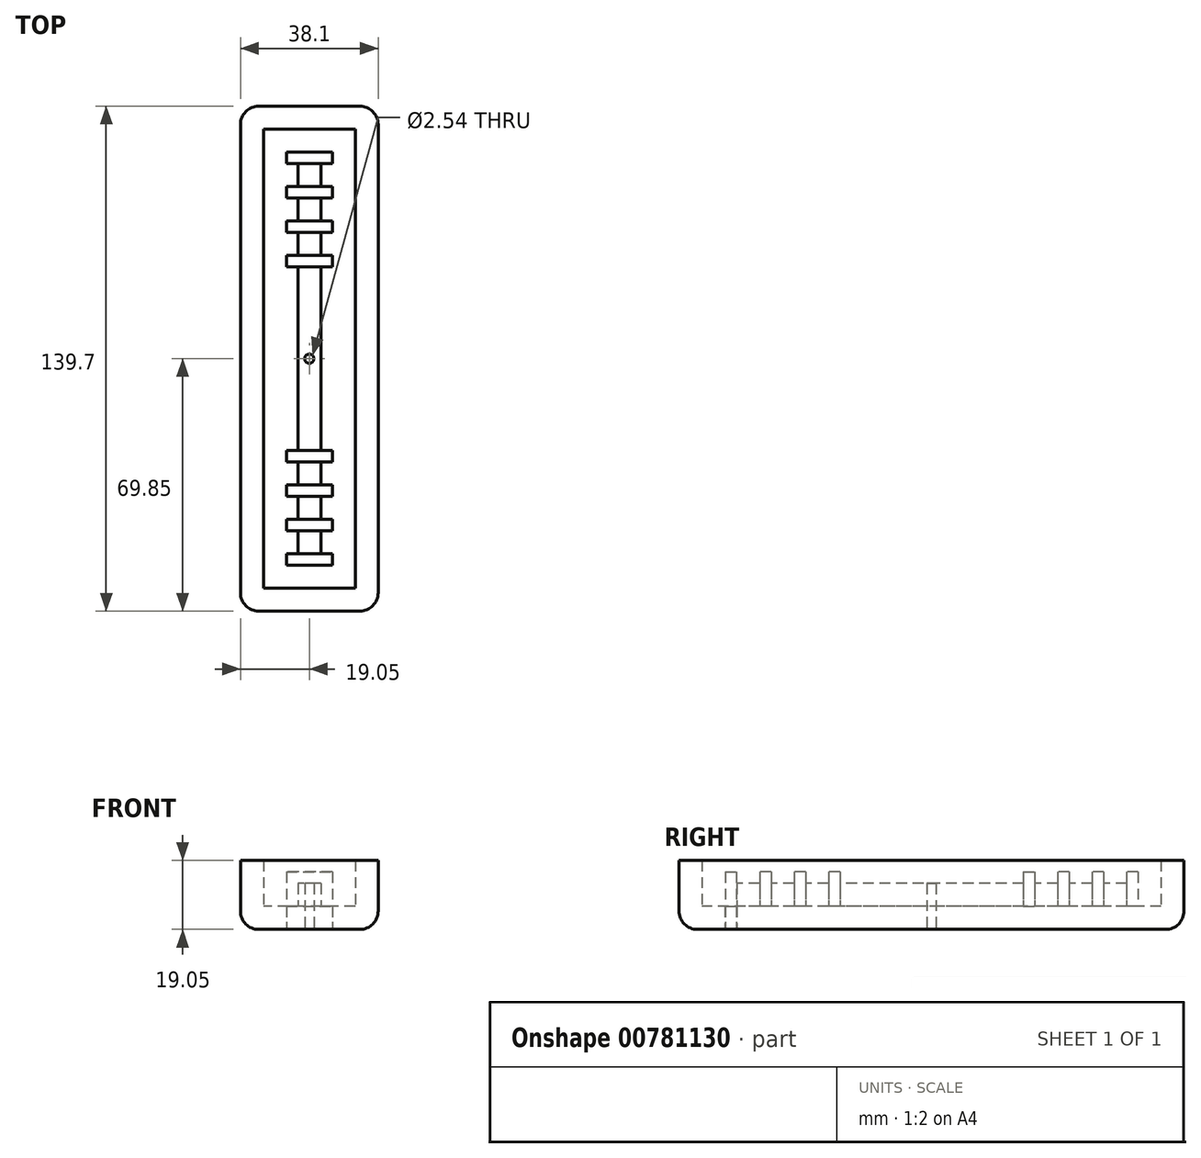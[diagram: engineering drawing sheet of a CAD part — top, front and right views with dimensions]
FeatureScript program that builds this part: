
annotation { "Feature Type Name" : "Feature", "Feature Type Description" : "" }
export const myFeature = defineFeature(function(context is Context, id is Id, definition is map)
    precondition{}
    {
        {
            var Q0;
            Q0=qCreatedBy(makeId("Top.planeOp"),FACE);
            var sketch = newSketch(context, id + "F0", { "sketchPlane" : qUnion([Q0])});
            skLineSegment(sketch, "E0.bottom", {"start": v(12.7, 63.5) * mm, "end": v(-12.7, 63.5) * mm});
            skLineSegment(sketch, "E0.top", {"start": v(12.7, -63.5) * mm, "end": v(-12.7, -63.5) * mm});
            skLineSegment(sketch, "E0.left", {"start": v(12.7, 63.5) * mm, "end": v(12.7, -63.5) * mm});
            skLineSegment(sketch, "E0.right", {"start": v(-12.7, 63.5) * mm, "end": v(-12.7, -63.5) * mm});
            skPoint(sketch, "E0.middle", {"position": v(0, 0) * mm});
            skLineSegment(sketch, "E1.bottom", {"start": v(19.05, 69.85) * mm, "end": v(-19.05, 69.85) * mm});
            skLineSegment(sketch, "E1.top", {"start": v(19.05, -69.85) * mm, "end": v(-19.05, -69.85) * mm});
            skLineSegment(sketch, "E1.left", {"start": v(19.05, 69.85) * mm, "end": v(19.05, -69.85) * mm});
            skLineSegment(sketch, "E1.right", {"start": v(-19.05, 69.85) * mm, "end": v(-19.05, -69.85) * mm});
            skLineSegment(sketch, "E2.bottom", {"start": v(3.18, 57.15) * mm, "end": v(-3.18, 57.15) * mm});
            skLineSegment(sketch, "E2.top", {"start": v(3.18, -57.15) * mm, "end": v(-3.18, -57.15) * mm});
            skLineSegment(sketch, "E2.left", {"start": v(3.18, 57.15) * mm, "end": v(3.18, -57.15) * mm});
            skLineSegment(sketch, "E2.right", {"start": v(-3.18, 57.15) * mm, "end": v(-3.18, -57.15) * mm});
            skLineSegment(sketch, "E3.bottom", {"start": v(6.35, 57.15) * mm, "end": v(-6.35, 57.15) * mm});
            skLineSegment(sketch, "E3.top", {"start": v(6.35, 53.98) * mm, "end": v(-6.35, 53.98) * mm});
            skLineSegment(sketch, "E3.left", {"start": v(6.35, 57.15) * mm, "end": v(6.35, 53.98) * mm});
            skLineSegment(sketch, "E3.right", {"start": v(-6.35, 57.15) * mm, "end": v(-6.35, 53.98) * mm});
            skPoint(sketch, "E3.middle", {"position": v(0, 55.56) * mm});
            skPoint(sketch, "E3.middle.positionSnap0", {"position": v(0, 57.15) * mm});
            skPoint(sketch, "E3.centerSnap0", {"position": v(0, 57.15) * mm});
            skLineSegment(sketch, "E4.bottom", {"start": v(-6.35, -57.15) * mm, "end": v(6.35, -57.15) * mm});
            skLineSegment(sketch, "E4.top", {"start": v(-6.35, -53.98) * mm, "end": v(6.35, -53.98) * mm});
            skLineSegment(sketch, "E4.left", {"start": v(-6.35, -57.15) * mm, "end": v(-6.35, -53.98) * mm});
            skLineSegment(sketch, "E4.right", {"start": v(6.35, -57.15) * mm, "end": v(6.35, -53.98) * mm});
            skPoint(sketch, "E4.middle", {"position": v(0, -55.56) * mm});
            skLineSegment(sketch, "E5.bottom", {"start": v(-6.35, 47.63) * mm, "end": v(6.35, 47.63) * mm});
            skLineSegment(sketch, "E5.top", {"start": v(-6.35, 44.45) * mm, "end": v(6.35, 44.45) * mm});
            skLineSegment(sketch, "E5.left", {"start": v(-6.35, 47.63) * mm, "end": v(-6.35, 44.45) * mm});
            skLineSegment(sketch, "E5.right", {"start": v(6.35, 47.63) * mm, "end": v(6.35, 44.45) * mm});
            skPoint(sketch, "E5.middle", {"position": v(0, 46.04) * mm});
            skLineSegment(sketch, "E6", {"start": v(3.18, 53.98) * mm, "end": v(3.18, 47.63) * mm});
            skLineSegment(sketch, "E7.bottom", {"start": v(6.35, 38.1) * mm, "end": v(-6.35, 38.1) * mm});
            skLineSegment(sketch, "E7.top", {"start": v(6.35, 34.93) * mm, "end": v(-6.35, 34.93) * mm});
            skLineSegment(sketch, "E7.left", {"start": v(6.35, 38.1) * mm, "end": v(6.35, 34.93) * mm});
            skLineSegment(sketch, "E7.right", {"start": v(-6.35, 38.1) * mm, "end": v(-6.35, 34.93) * mm});
            skPoint(sketch, "E7.middle", {"position": v(0, 36.51) * mm});
            skLineSegment(sketch, "E8", {"start": v(3.18, 44.45) * mm, "end": v(3.18, 38.1) * mm});
            skLineSegment(sketch, "E9.bottom", {"start": v(6.35, 25.4) * mm, "end": v(-6.35, 25.4) * mm});
            skLineSegment(sketch, "E9.top", {"start": v(6.35, 28.58) * mm, "end": v(-6.35, 28.58) * mm});
            skLineSegment(sketch, "E9.left", {"start": v(6.35, 25.4) * mm, "end": v(6.35, 28.58) * mm});
            skLineSegment(sketch, "E9.right", {"start": v(-6.35, 25.4) * mm, "end": v(-6.35, 28.58) * mm});
            skPoint(sketch, "E9.middle", {"position": v(0, 26.99) * mm});
            skLineSegment(sketch, "E10", {"start": v(3.18, 34.93) * mm, "end": v(3.18, 28.58) * mm});
            skLineSegment(sketch, "E11.bottom", {"start": v(6.38, -25.35) * mm, "end": v(-6.32, -25.35) * mm});
            skLineSegment(sketch, "E11.top", {"start": v(6.38, -28.53) * mm, "end": v(-6.32, -28.53) * mm});
            skLineSegment(sketch, "E11.left", {"start": v(6.38, -25.35) * mm, "end": v(6.38, -28.53) * mm});
            skLineSegment(sketch, "E11.right", {"start": v(-6.32, -25.35) * mm, "end": v(-6.32, -28.53) * mm});
            skLineSegment(sketch, "E12.bottom", {"start": v(-6.32, -34.88) * mm, "end": v(6.38, -34.88) * mm});
            skLineSegment(sketch, "E12.top", {"start": v(-6.32, -38.05) * mm, "end": v(6.38, -38.05) * mm});
            skLineSegment(sketch, "E12.left", {"start": v(-6.32, -34.88) * mm, "end": v(-6.32, -38.05) * mm});
            skLineSegment(sketch, "E12.right", {"start": v(6.38, -34.88) * mm, "end": v(6.38, -38.05) * mm});
            skLineSegment(sketch, "E13.bottom", {"start": v(6.38, -44.4) * mm, "end": v(-6.32, -44.4) * mm});
            skLineSegment(sketch, "E13.top", {"start": v(6.38, -47.58) * mm, "end": v(-6.32, -47.58) * mm});
            skLineSegment(sketch, "E13.left", {"start": v(6.38, -44.4) * mm, "end": v(6.38, -47.58) * mm});
            skLineSegment(sketch, "E13.right", {"start": v(-6.32, -44.4) * mm, "end": v(-6.32, -47.58) * mm});
            skLineSegment(sketch, "E14.bottom", {"start": v(6.38, -57.1) * mm, "end": v(-6.32, -57.1) * mm});
            skLineSegment(sketch, "E14.top", {"start": v(6.38, -53.93) * mm, "end": v(-6.32, -53.93) * mm});
            skLineSegment(sketch, "E14.left", {"start": v(6.38, -57.1) * mm, "end": v(6.38, -53.93) * mm});
            skLineSegment(sketch, "E14.right", {"start": v(-6.32, -57.1) * mm, "end": v(-6.32, -53.93) * mm});
            skCircle(sketch, "E15", {"center": v(0, 0) * mm, "radius": 1.27 * mm});
            skSolve(sketch);
        }
        {
            var Q0;
            Q0=makeQuery(id+"F0.imprint","IMPRINT",FACE,{"disambiguationData":[TD([[makeQuery(id+"F0.imprint","IMPRINT",EDGE,{"derivedFrom":sQuery(id+"F0.wireOp",EDGE,"E0.bottom")}),-1.0]])]});
            extrude(context, id + "F1", {"entities" : qUnion([Q0]), "depth" : 19.05 * mm, "offsetDistance" : 25.4 * mm});
        }
        {
            var Q0;
            Q0=makeQuery(id+"F0.imprint","IMPRINT",FACE,{"disambiguationData":[TD([[makeQuery(id+"F0.imprint","IMPRINT",EDGE,{"derivedFrom":sQuery(id+"F0.wireOp",EDGE,"E0.bottom")}),1.0]])]});
            extrude(context, id + "F2", {"entities" : qUnion([Q0]), "operationType" : NewBodyOperationType.ADD, "depth" : 6.35 * mm, "offsetDistance" : 25.4 * mm});
        }
        {
            var Q0;
            Q0=makeQuery(id+"F0.imprint","IMPRINT",FACE,{"disambiguationData":[TD([[makeQuery(id+"F0.imprint","IMPRINT",EDGE,{"derivedFrom":sQuery(id+"F0.wireOp",EDGE,"E15")}),-1.0]])]});
            var Q1;
            {var subQ0=sQuery(id+"F0.wireOp",EDGE,"E7.top");var subQ1=sQuery(id+"F0.wireOp",EDGE,"E2.left");var subQ2=makeQuery(id+"F0.imprint","INTERSECT",VERTEX,{"derivedFrom":[subQ1,subQ0]});Q1=makeQuery(id+"F0.imprint","IMPRINT",FACE,{"disambiguationData":[TD([[makeQuery(id+"F0.imprint","IMPRINT",EDGE,{"disambiguationData":[TD([[subQ2,-1.0]])],"derivedFrom":subQ1}),-1.0]])]});}
            var Q2;
            {var subQ0=sQuery(id+"F0.wireOp",EDGE,"E7.bottom");var subQ1=sQuery(id+"F0.wireOp",EDGE,"E2.left");var subQ2=makeQuery(id+"F0.imprint","INTERSECT",VERTEX,{"derivedFrom":[subQ1,subQ0]});Q2=makeQuery(id+"F0.imprint","IMPRINT",FACE,{"disambiguationData":[TD([[makeQuery(id+"F0.imprint","IMPRINT",EDGE,{"disambiguationData":[TD([[subQ2,1.0]])],"derivedFrom":subQ1}),-1.0]])]});}
            var Q3;
            {var subQ0=sQuery(id+"F0.wireOp",EDGE,"E3.top");var subQ1=sQuery(id+"F0.wireOp",EDGE,"E2.left");var subQ2=makeQuery(id+"F0.imprint","INTERSECT",VERTEX,{"derivedFrom":[subQ1,subQ0]});Q3=makeQuery(id+"F0.imprint","IMPRINT",FACE,{"disambiguationData":[TD([[makeQuery(id+"F0.imprint","IMPRINT",EDGE,{"disambiguationData":[TD([[subQ2,-1.0]])],"derivedFrom":subQ1}),-1.0]])]});}
            var Q4;
            {var subQ0=sQuery(id+"F0.wireOp",EDGE,"E11.top");var subQ1=sQuery(id+"F0.wireOp",EDGE,"E2.left");var subQ2=makeQuery(id+"F0.imprint","INTERSECT",VERTEX,{"derivedFrom":[subQ1,subQ0]});Q4=makeQuery(id+"F0.imprint","IMPRINT",FACE,{"disambiguationData":[TD([[makeQuery(id+"F0.imprint","IMPRINT",EDGE,{"disambiguationData":[TD([[subQ2,-1.0]])],"derivedFrom":subQ1}),-1.0]])]});}
            var Q5;
            {var subQ0=sQuery(id+"F0.wireOp",EDGE,"E13.bottom");var subQ1=sQuery(id+"F0.wireOp",EDGE,"E2.left");var subQ2=makeQuery(id+"F0.imprint","INTERSECT",VERTEX,{"derivedFrom":[subQ1,subQ0]});Q5=makeQuery(id+"F0.imprint","IMPRINT",FACE,{"disambiguationData":[TD([[makeQuery(id+"F0.imprint","IMPRINT",EDGE,{"disambiguationData":[TD([[subQ2,1.0]])],"derivedFrom":subQ1}),-1.0]])]});}
            var Q6;
            {var subQ0=sQuery(id+"F0.wireOp",EDGE,"E13.top");var subQ1=sQuery(id+"F0.wireOp",EDGE,"E2.left");var subQ2=makeQuery(id+"F0.imprint","INTERSECT",VERTEX,{"derivedFrom":[subQ1,subQ0]});Q6=makeQuery(id+"F0.imprint","IMPRINT",FACE,{"disambiguationData":[TD([[makeQuery(id+"F0.imprint","IMPRINT",EDGE,{"disambiguationData":[TD([[subQ2,-1.0]])],"derivedFrom":subQ1}),-1.0]])]});}
            extrude(context, id + "F3", {"entities" : qUnion([Q0, Q1, Q2, Q3, Q4, Q5, Q6]), "operationType" : NewBodyOperationType.ADD, "depth" : 12.7 * mm, "offsetDistance" : 25.4 * mm});
        }
        {
            var Q0;
            {var subQ0=sQuery(id+"F0.wireOp",EDGE,"E2.bottom");Q0=makeQuery(id+"F0.imprint","IMPRINT",FACE,{"disambiguationData":[TD([[makeQuery(id+"F0.imprint","IMPRINT",EDGE,{"derivedFrom":subQ0}),1.0]])]});}
            var Q1;
            {var subQ5=sQuery(id+"F0.wireOp",EDGE,"E3.left");Q1=makeQuery(id+"F0.imprint","IMPRINT",FACE,{"disambiguationData":[TD([[makeQuery(id+"F0.imprint","IMPRINT",EDGE,{"derivedFrom":subQ5}),-1.0]])]});}
            var Q2;
            {var subQ5=sQuery(id+"F0.wireOp",EDGE,"E3.right");Q2=makeQuery(id+"F0.imprint","IMPRINT",FACE,{"disambiguationData":[TD([[makeQuery(id+"F0.imprint","IMPRINT",EDGE,{"derivedFrom":subQ5}),1.0]])]});}
            var Q3;
            {var subQ5=sQuery(id+"F0.wireOp",EDGE,"E5.left");Q3=makeQuery(id+"F0.imprint","IMPRINT",FACE,{"disambiguationData":[TD([[makeQuery(id+"F0.imprint","IMPRINT",EDGE,{"derivedFrom":subQ5}),1.0]])]});}
            var Q4;
            {var subQ0=sQuery(id+"F0.wireOp",EDGE,"E5.top");var subQ1=sQuery(id+"F0.wireOp",EDGE,"E2.left");var subQ2=makeQuery(id+"F0.imprint","INTERSECT",VERTEX,{"derivedFrom":[subQ1,subQ0]});Q4=makeQuery(id+"F0.imprint","IMPRINT",FACE,{"disambiguationData":[TD([[makeQuery(id+"F0.imprint","IMPRINT",EDGE,{"disambiguationData":[TD([[subQ2,1.0]])],"derivedFrom":subQ1}),-1.0]])]});}
            var Q5;
            {var subQ5=sQuery(id+"F0.wireOp",EDGE,"E5.right");Q5=makeQuery(id+"F0.imprint","IMPRINT",FACE,{"disambiguationData":[TD([[makeQuery(id+"F0.imprint","IMPRINT",EDGE,{"derivedFrom":subQ5}),-1.0]])]});}
            var Q6;
            {var subQ5=sQuery(id+"F0.wireOp",EDGE,"E7.left");Q6=makeQuery(id+"F0.imprint","IMPRINT",FACE,{"disambiguationData":[TD([[makeQuery(id+"F0.imprint","IMPRINT",EDGE,{"derivedFrom":subQ5}),-1.0]])]});}
            var Q7;
            {var subQ0=sQuery(id+"F0.wireOp",EDGE,"E7.bottom");var subQ1=sQuery(id+"F0.wireOp",EDGE,"E2.left");var subQ2=makeQuery(id+"F0.imprint","INTERSECT",VERTEX,{"derivedFrom":[subQ1,subQ0]});Q7=makeQuery(id+"F0.imprint","IMPRINT",FACE,{"disambiguationData":[TD([[makeQuery(id+"F0.imprint","IMPRINT",EDGE,{"disambiguationData":[TD([[subQ2,-1.0]])],"derivedFrom":subQ1}),-1.0]])]});}
            var Q8;
            {var subQ5=sQuery(id+"F0.wireOp",EDGE,"E7.right");Q8=makeQuery(id+"F0.imprint","IMPRINT",FACE,{"disambiguationData":[TD([[makeQuery(id+"F0.imprint","IMPRINT",EDGE,{"derivedFrom":subQ5}),1.0]])]});}
            var Q9;
            {var subQ5=sQuery(id+"F0.wireOp",EDGE,"E9.right");Q9=makeQuery(id+"F0.imprint","IMPRINT",FACE,{"disambiguationData":[TD([[makeQuery(id+"F0.imprint","IMPRINT",EDGE,{"derivedFrom":subQ5}),-1.0]])]});}
            var Q10;
            {var subQ0=sQuery(id+"F0.wireOp",EDGE,"E9.bottom");var subQ1=sQuery(id+"F0.wireOp",EDGE,"E2.left");var subQ2=makeQuery(id+"F0.imprint","INTERSECT",VERTEX,{"derivedFrom":[subQ1,subQ0]});Q10=makeQuery(id+"F0.imprint","IMPRINT",FACE,{"disambiguationData":[TD([[makeQuery(id+"F0.imprint","IMPRINT",EDGE,{"disambiguationData":[TD([[subQ2,1.0]])],"derivedFrom":subQ1}),-1.0]])]});}
            var Q11;
            {var subQ5=sQuery(id+"F0.wireOp",EDGE,"E9.left");Q11=makeQuery(id+"F0.imprint","IMPRINT",FACE,{"disambiguationData":[TD([[makeQuery(id+"F0.imprint","IMPRINT",EDGE,{"derivedFrom":subQ5}),1.0]])]});}
            var Q12;
            {var subQ0=sQuery(id+"F0.wireOp",EDGE,"E11.bottom");var subQ1=sQuery(id+"F0.wireOp",EDGE,"E2.left");var subQ2=makeQuery(id+"F0.imprint","INTERSECT",VERTEX,{"derivedFrom":[subQ1,subQ0]});Q12=makeQuery(id+"F0.imprint","IMPRINT",FACE,{"disambiguationData":[TD([[makeQuery(id+"F0.imprint","IMPRINT",EDGE,{"disambiguationData":[TD([[subQ2,-1.0]])],"derivedFrom":subQ1}),-1.0]])]});}
            var Q13;
            {var subQ5=sQuery(id+"F0.wireOp",EDGE,"E11.right");Q13=makeQuery(id+"F0.imprint","IMPRINT",FACE,{"disambiguationData":[TD([[makeQuery(id+"F0.imprint","IMPRINT",EDGE,{"derivedFrom":subQ5}),1.0]])]});}
            var Q14;
            {var subQ5=sQuery(id+"F0.wireOp",EDGE,"E11.left");Q14=makeQuery(id+"F0.imprint","IMPRINT",FACE,{"disambiguationData":[TD([[makeQuery(id+"F0.imprint","IMPRINT",EDGE,{"derivedFrom":subQ5}),-1.0]])]});}
            var Q15;
            {var subQ5=sQuery(id+"F0.wireOp",EDGE,"E12.right");Q15=makeQuery(id+"F0.imprint","IMPRINT",FACE,{"disambiguationData":[TD([[makeQuery(id+"F0.imprint","IMPRINT",EDGE,{"derivedFrom":subQ5}),-1.0]])]});}
            var Q16;
            {var subQ0=sQuery(id+"F0.wireOp",EDGE,"E12.bottom");var subQ1=sQuery(id+"F0.wireOp",EDGE,"E2.left");var subQ2=makeQuery(id+"F0.imprint","INTERSECT",VERTEX,{"derivedFrom":[subQ1,subQ0]});Q16=makeQuery(id+"F0.imprint","IMPRINT",FACE,{"disambiguationData":[TD([[makeQuery(id+"F0.imprint","IMPRINT",EDGE,{"disambiguationData":[TD([[subQ2,-1.0]])],"derivedFrom":subQ1}),-1.0]])]});}
            var Q17;
            {var subQ5=sQuery(id+"F0.wireOp",EDGE,"E12.left");Q17=makeQuery(id+"F0.imprint","IMPRINT",FACE,{"disambiguationData":[TD([[makeQuery(id+"F0.imprint","IMPRINT",EDGE,{"derivedFrom":subQ5}),1.0]])]});}
            var Q18;
            {var subQ0=sQuery(id+"F0.wireOp",EDGE,"E13.bottom");var subQ1=sQuery(id+"F0.wireOp",EDGE,"E2.left");var subQ2=makeQuery(id+"F0.imprint","INTERSECT",VERTEX,{"derivedFrom":[subQ1,subQ0]});Q18=makeQuery(id+"F0.imprint","IMPRINT",FACE,{"disambiguationData":[TD([[makeQuery(id+"F0.imprint","IMPRINT",EDGE,{"disambiguationData":[TD([[subQ2,-1.0]])],"derivedFrom":subQ1}),-1.0]])]});}
            var Q19;
            {var subQ0=sQuery(id+"F0.wireOp",EDGE,"E4.top");var subQ1=sQuery(id+"F0.wireOp",EDGE,"E2.left");var subQ2=makeQuery(id+"F0.imprint","INTERSECT",VERTEX,{"derivedFrom":[subQ1,subQ0]});Q19=makeQuery(id+"F0.imprint","IMPRINT",FACE,{"disambiguationData":[TD([[makeQuery(id+"F0.imprint","IMPRINT",EDGE,{"disambiguationData":[TD([[subQ2,-1.0]])],"derivedFrom":subQ1}),-1.0]])]});}
            var Q20;
            {var subQ5=sQuery(id+"F0.wireOp",EDGE,"E13.left");Q20=makeQuery(id+"F0.imprint","IMPRINT",FACE,{"disambiguationData":[TD([[makeQuery(id+"F0.imprint","IMPRINT",EDGE,{"derivedFrom":subQ5}),-1.0]])]});}
            var Q21;
            {var subQ0=sQuery(id+"F0.wireOp",EDGE,"E4.top");var subQ1=sQuery(id+"F0.wireOp",EDGE,"E2.left");var subQ2=makeQuery(id+"F0.imprint","INTERSECT",VERTEX,{"derivedFrom":[subQ1,subQ0]});Q21=makeQuery(id+"F0.imprint","IMPRINT",FACE,{"disambiguationData":[TD([[makeQuery(id+"F0.imprint","IMPRINT",EDGE,{"disambiguationData":[TD([[subQ2,-1.0]])],"derivedFrom":subQ1}),1.0]])]});}
            var Q22;
            {var subQ0=sQuery(id+"F0.wireOp",EDGE,"E4.top");var subQ1=sQuery(id+"F0.wireOp",EDGE,"E2.right");var subQ2=makeQuery(id+"F0.imprint","INTERSECT",VERTEX,{"derivedFrom":[subQ1,subQ0]});Q22=makeQuery(id+"F0.imprint","IMPRINT",FACE,{"disambiguationData":[TD([[makeQuery(id+"F0.imprint","IMPRINT",EDGE,{"disambiguationData":[TD([[subQ2,-1.0]])],"derivedFrom":subQ1}),-1.0]])]});}
            var Q23;
            {var subQ5=sQuery(id+"F0.wireOp",EDGE,"E13.right");Q23=makeQuery(id+"F0.imprint","IMPRINT",FACE,{"disambiguationData":[TD([[makeQuery(id+"F0.imprint","IMPRINT",EDGE,{"derivedFrom":subQ5}),1.0]])]});}
            extrude(context, id + "F4", {"entities" : qUnion([Q0, Q1, Q2, Q3, Q4, Q5, Q6, Q7, Q8, Q9, Q10, Q11, Q12, Q13, Q14, Q15, Q16, Q17, Q18, Q19, Q20, Q21, Q22, Q23]), "operationType" : NewBodyOperationType.ADD, "depth" : 15.88 * mm, "offsetDistance" : 25.4 * mm});
        }
        {
            var Q0;
            Q0=makeQuery(id+"F1.opExtrude","SWEPT_EDGE",EDGE,{"disambiguationData":[OSD([sQuery(id+"F0.wireOp",EDGE,"E1.bottom"),sQuery(id+"F0.wireOp",EDGE,"E1.left")])]});
            fillet(context, id + "F5", {"entities" : qUnion([Q0]), "radius" : 5.08 * mm, "tangentPropagation" : true, "allowEdgeOverflow" : false});
        }
        {
            var Q0;
            Q0=makeQuery(id+"F1.opExtrude","SWEPT_EDGE",EDGE,{"disambiguationData":[OSD([sQuery(id+"F0.wireOp",EDGE,"E1.bottom"),sQuery(id+"F0.wireOp",EDGE,"E1.right")])]});
            fillet(context, id + "F6", {"entities" : qUnion([Q0]), "radius" : 5.08 * mm, "tangentPropagation" : true, "allowEdgeOverflow" : false});
        }
        {
            var Q0;
            Q0=makeQuery(id+"F1.opExtrude","SWEPT_EDGE",EDGE,{"disambiguationData":[OSD([sQuery(id+"F0.wireOp",EDGE,"E1.top"),sQuery(id+"F0.wireOp",EDGE,"E1.left")])]});
            fillet(context, id + "F7", {"entities" : qUnion([Q0]), "radius" : 5.08 * mm, "tangentPropagation" : true, "allowEdgeOverflow" : false});
        }
        {
            var Q0;
            Q0=makeQuery(id+"F1.opExtrude","SWEPT_EDGE",EDGE,{"disambiguationData":[OSD([sQuery(id+"F0.wireOp",EDGE,"E1.top"),sQuery(id+"F0.wireOp",EDGE,"E1.right")])]});
            fillet(context, id + "F8", {"entities" : qUnion([Q0]), "radius" : 5.08 * mm, "tangentPropagation" : true, "allowEdgeOverflow" : false});
        }
        {
            var Q0;
            Q0=makeQuery(id+"F1.opExtrude","CAP_EDGE",EDGE,{"disambiguationData":[OSD([sQuery(id+"F0.wireOp",EDGE,"E1.top")])],"isStart":true});
            fillet(context, id + "F9", {"entities" : qUnion([Q0]), "radius" : 5.08 * mm, "tangentPropagation" : true, "allowEdgeOverflow" : false});
        }
    });
